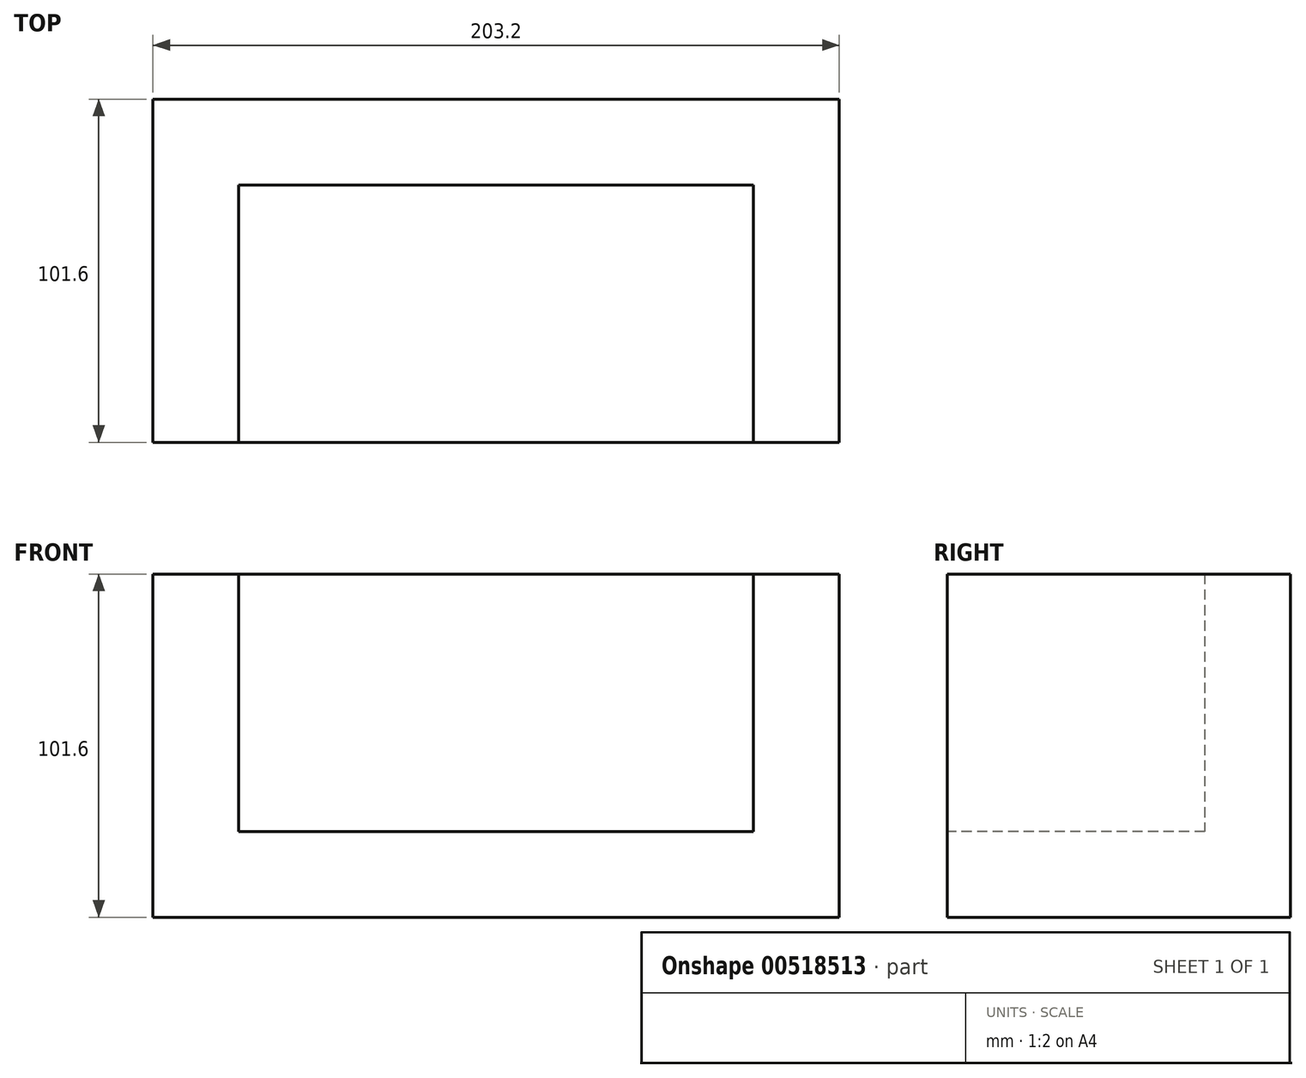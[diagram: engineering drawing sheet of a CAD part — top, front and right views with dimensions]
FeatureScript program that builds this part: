
annotation { "Feature Type Name" : "Feature", "Feature Type Description" : "" }
export const myFeature = defineFeature(function(context is Context, id is Id, definition is map)
    precondition{}
    {
        {
            var Q0;
            Q0=qCreatedBy(makeId("Front.planeOp"),FACE);
            var sketch = newSketch(context, id + "F0", { "sketchPlane" : qUnion([Q0])});
            skLineSegment(sketch, "E0.bottom", {"start": v(-164.88, 4.83) * mm, "end": v(38.32, 4.83) * mm});
            skLineSegment(sketch, "E0.top", {"start": v(-164.88, -96.77) * mm, "end": v(38.32, -96.77) * mm});
            skLineSegment(sketch, "E0.left", {"start": v(-164.88, 4.83) * mm, "end": v(-164.88, -96.77) * mm});
            skLineSegment(sketch, "E0.right", {"start": v(38.32, 4.83) * mm, "end": v(38.32, -96.77) * mm});
            skSolve(sketch);
        }
        {
            var Q0;
            Q0=qSketchRegion(id+"F0",true);
            extrude(context, id + "F1", {"entities" : qUnion([Q0]), "depth" : 101.6 * mm});
        }
        {
            var Q0;
            Q0=makeQuery(id+"F1.opExtrude","CAP_FACE",FACE,{"disambiguationData":[OSD([sQuery(id+"F0.wireOp",EDGE,"E0.bottom"),sQuery(id+"F0.wireOp",EDGE,"E0.top"),sQuery(id+"F0.wireOp",EDGE,"E0.left"),sQuery(id+"F0.wireOp",EDGE,"E0.right")])],"isStart":false});
            var sketch = newSketch(context, id + "F2", { "sketchPlane" : qUnion([Q0])});
            skLineSegment(sketch, "E1.bottom", {"start": v(-139.48, 4.83) * mm, "end": v(12.92, 4.83) * mm});
            skLineSegment(sketch, "E1.top", {"start": v(-139.48, -71.37) * mm, "end": v(12.92, -71.37) * mm});
            skLineSegment(sketch, "E1.left", {"start": v(-139.48, 4.83) * mm, "end": v(-139.48, -71.37) * mm});
            skLineSegment(sketch, "E1.right", {"start": v(12.92, 4.83) * mm, "end": v(12.92, -71.37) * mm});
            skSolve(sketch);
        }
        {
            var Q0;
            Q0=qSketchRegion(id+"F2",true);
            extrude(context, id + "F3", {"entities" : qUnion([Q0]), "operationType" : NewBodyOperationType.REMOVE, "oppositeDirection" : true, "depth" : 76.2 * mm});
        }
    });
